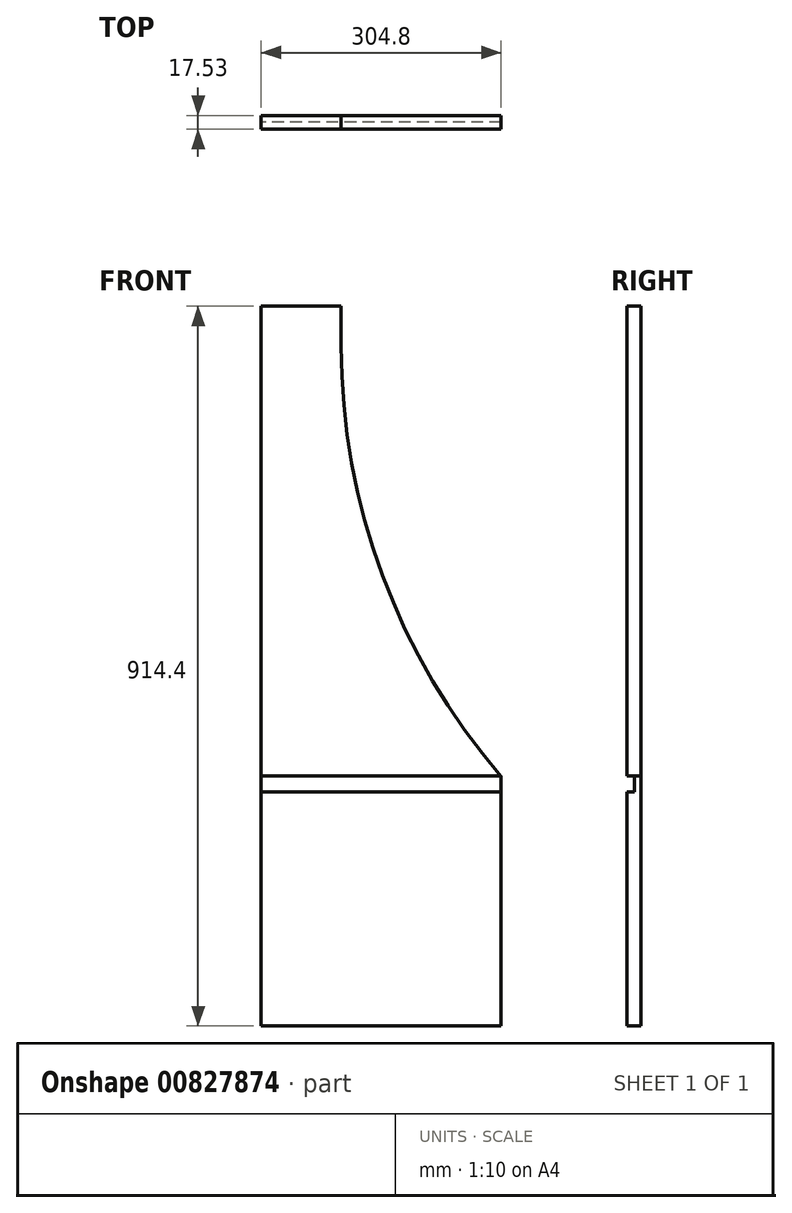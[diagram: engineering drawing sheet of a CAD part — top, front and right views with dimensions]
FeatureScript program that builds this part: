
annotation { "Feature Type Name" : "Feature", "Feature Type Description" : "" }
export const myFeature = defineFeature(function(context is Context, id is Id, definition is map)
    precondition{}
    {
        {
            var Q0;
            Q0=qCreatedBy(makeId("Front.planeOp"),FACE);
            var sketch = newSketch(context, id + "F0", { "sketchPlane" : qUnion([Q0])});
            skLineSegment(sketch, "E0", {"start": v(-92.77, 146.48) * mm, "end": v(-92.77, -767.92) * mm});
            skLineSegment(sketch, "E1", {"start": v(-92.77, -767.92) * mm, "end": v(212.03, -767.92) * mm});
            skLineSegment(sketch, "E2", {"start": v(212.03, -767.92) * mm, "end": v(212.03, -450.42) * mm});
            skLineSegment(sketch, "E3", {"start": v(-92.77, 146.48) * mm, "end": v(8.83, 146.48) * mm});
            skLineSegment(sketch, "E4", {"start": v(8.83, 146.48) * mm, "end": v(8.83, 95.68) * mm});
            skLineSegment(sketch, "E5.bottom", {"start": v(212.03, -450.42) * mm, "end": v(-92.77, -450.42) * mm});
            skLineSegment(sketch, "E5.top", {"start": v(212.03, -470.74) * mm, "end": v(-92.77, -470.74) * mm});
            skLineSegment(sketch, "E5.left", {"start": v(212.03, -450.42) * mm, "end": v(212.03, -470.74) * mm});
            skLineSegment(sketch, "E5.right", {"start": v(-92.77, -450.42) * mm, "end": v(-92.77, -470.74) * mm});
            skArc(sketch, "E6", {"start": v(8.83, 95.68) * mm, "mid": v(61.28, -195.66) * mm, "end": v(212.03, -450.42) * mm});
            skSolve(sketch);
        }
        {
            var Q0;
            {var subQ1=sQuery(id+"F0.wireOp",EDGE,"E3");Q0=makeQuery(id+"F0.imprint","IMPRINT",FACE,{"disambiguationData":[TD([[makeQuery(id+"F0.imprint","IMPRINT",EDGE,{"derivedFrom":subQ1}),-1.0]])]});}
            extrude(context, id + "F1", {"entities" : qUnion([Q0]), "depth" : 17.53 * mm, "offsetDistance" : 25.4 * mm});
        }
        {
            var Q0;
            Q0=makeQuery(id+"F0.imprint","IMPRINT",FACE,{"disambiguationData":[TD([[makeQuery(id+"F0.imprint","IMPRINT",EDGE,{"derivedFrom":sQuery(id+"F0.wireOp",EDGE,"E5.bottom")}),1.0]])]});
            extrude(context, id + "F2", {"entities" : qUnion([Q0]), "operationType" : NewBodyOperationType.ADD, "depth" : 8.25 * mm, "offsetDistance" : 25.4 * mm});
        }
        {
            var Q0;
            {var subQ0=sQuery(id+"F0.wireOp",EDGE,"E1");Q0=makeQuery(id+"F0.imprint","IMPRINT",FACE,{"disambiguationData":[TD([[makeQuery(id+"F0.imprint","IMPRINT",EDGE,{"derivedFrom":subQ0}),1.0]])]});}
            extrude(context, id + "F3", {"entities" : qUnion([Q0]), "operationType" : NewBodyOperationType.ADD, "depth" : 17.53 * mm, "offsetDistance" : 25.4 * mm});
        }
    });
